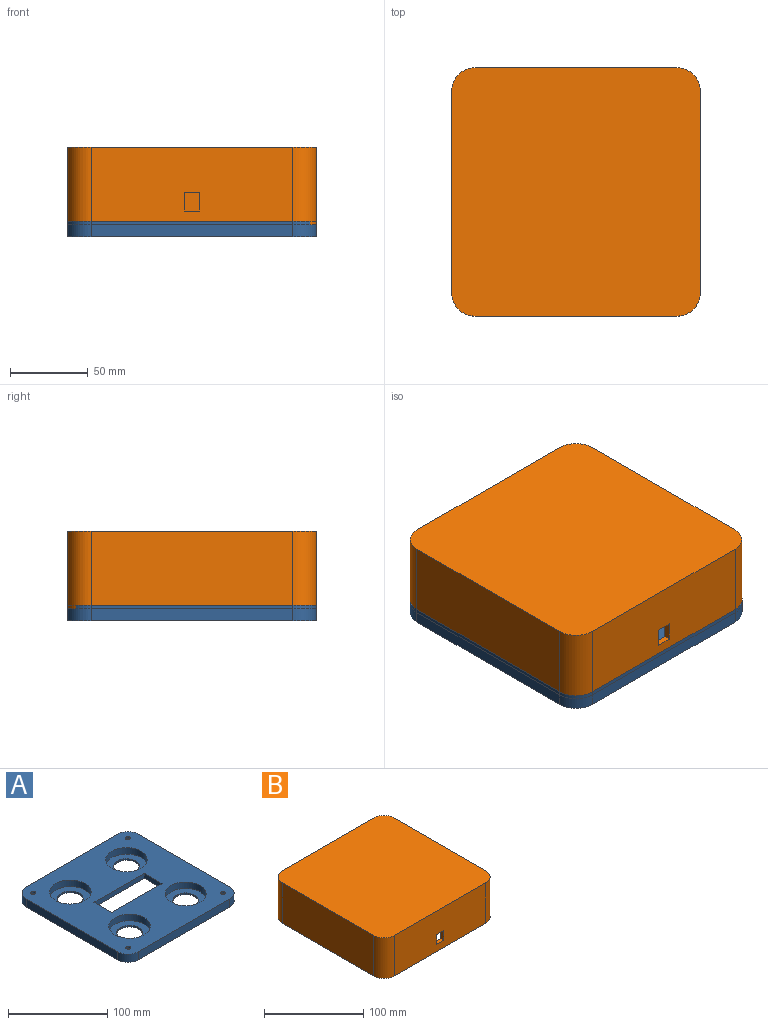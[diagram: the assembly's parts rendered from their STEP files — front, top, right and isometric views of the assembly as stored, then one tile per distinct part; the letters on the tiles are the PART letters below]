
ASSEMBLY  parts=2 mates=1
PART A: 53 faces, bbox 160x160x10 mm
  f0: plane 7x4.86mm, normal (0,-1,0), area 14.8mm2, adj f25,f44,f45,f46,f47,f52
  f1: plane 7x4.81mm, normal (0,1,0), area 14.7mm2, adj f2,f25,f44,f46,f48,f52
  f2: plane 25.5x6mm, normal (1,0,0), area 77.2mm2, adj f1,f3,f6,f24,f46,f52
  f3: plane 71.5x6mm, normal (0,-1,0), area 428.9mm2, adj f2,f23,f24,f45,f46,f52
  f4: cylinder r=21mm len=2.5mm, axis (0,0,-1), area 1.2mm2, adj f25,f30
  f5: cylinder r=21mm len=1.77mm, axis (0,0,-1), area 0.4mm2, adj f25,f29
  f6: plane 71.5x6mm, normal (0,1,0), area 429mm2, adj f2,f23,f24,f52
  f7: plane 130x10mm, normal (1,0,0), area 1300mm2, adj f8,f14,f24,f25
  f8: cylinder r=15mm len=15mm, axis (0,0,-1), area 235.6mm2, adj f7,f9,f24,f25
  f9: plane 130x10mm, normal (0,1,0), area 1300mm2, adj f8,f10,f24,f25
  f10: cylinder r=15mm len=15mm, axis (0,0,-1), area 235.6mm2, adj f9,f11,f24,f25
  f11: plane 130x10mm, normal (-1,0,0), area 1300mm2, adj f10,f12,f24,f25
  f12: cylinder r=15mm len=15mm, axis (0,0,-1), area 235.6mm2, adj f11,f13,f24,f25
  f13: plane 130x10mm, normal (0,-1,0), area 1300mm2, adj f12,f14,f24,f25
  f14: cylinder r=15mm len=15mm, axis (0,0,-1), area 235.6mm2, adj f7,f13,f24,f25
  f15: cylinder r=2.5mm len=5mm, axis (0,0,-1), area 39.3mm2, adj f24,f37
  f16: cylinder r=2.5mm len=5mm, axis (0,0,-1), area 39.3mm2, adj f24,f41
  f17: cylinder r=2.5mm len=5mm, axis (0,0,-1), area 39.3mm2, adj f24,f43
  f18: cylinder r=20.75mm len=41.5mm, axis (0,0,-1), area 1043mm2, adj f24,f34
  f19: cylinder r=21mm len=42mm, axis (0,0,-1), area 1055.6mm2, adj f24,f28
  f20: cylinder r=21mm len=42mm, axis (0,0,-1), area 1055.6mm2, adj f24,f26
  f21: cylinder r=21mm len=42mm, axis (0,0,-1), area 1055.6mm2, adj f24,f32
  f22: cylinder r=2.5mm len=5mm, axis (0,0,-1), area 39.3mm2, adj f24,f39
  f23: plane 25.5x6mm, normal (-1,0,0), area 153mm2, adj f3,f6,f24,f52
  f24: plane 160x160mm, normal (0,0,1), area 17996.1mm2, adj f2,f3,f6,f7,f8,f9,f10,f11
  f25: plane 160x160mm, normal (0,0,-1), area 20256.1mm2, adj f0,f1,f4,f5,f7,f8,f9,f10
  f26: plane 42x42mm, normal (0,0,1), area 863mm2, adj f20,f27
  f27: cone r=13mm half-angle=3deg, axis (0,0,-1), area 162.9mm2, adj f25,f26
  f28: plane 42x42mm, normal (0,0,1), area 863mm2, adj f19,f31
  f29: plane 1.77x0.36mm, normal (-0.04,-1,-0.05), area 0.4mm2, adj f5,f25
  f30: plane 2.5x0.71mm, normal (0.06,-1,-0.05), area 1.2mm2, adj f4,f25
  f31: cone r=13mm half-angle=3deg, axis (0,0,-1), area 162.9mm2, adj f25,f28
  f32: plane 42x42mm, normal (0,0,1), area 863mm2, adj f21,f33
  f33: cone r=13mm half-angle=3deg, axis (0,0,-1), area 162.9mm2, adj f25,f32
  f34: plane 41.5x41.5mm, normal (0,0,1), area 830.2mm2, adj f18,f35
  f35: cone r=13mm half-angle=3deg, axis (0,0,-1), area 162.9mm2, adj f25,f34
  f36: cylinder r=1.5mm len=7.5mm, axis (0,0,-1), area 70.7mm2, adj f25,f37
  f37: plane 5x5mm, normal (0,0,1), area 12.6mm2, adj f15,f36
  f38: cylinder r=1.5mm len=7.5mm, axis (0,0,-1), area 70.7mm2, adj f25,f39
  f39: plane 5x5mm, normal (0,0,1), area 12.6mm2, adj f22,f38
  f40: cylinder r=1.5mm len=7.5mm, axis (0,0,-1), area 70.7mm2, adj f25,f41
  f41: plane 5x5mm, normal (0,0,1), area 12.6mm2, adj f16,f40
  f42: cylinder r=1.5mm len=7.5mm, axis (0,0,-1), area 70.7mm2, adj f25,f43
  f43: plane 5x5mm, normal (0,0,1), area 12.6mm2, adj f17,f42
  f44: plane 25.33x7mm, normal (1,0,0), area 177.3mm2, adj f0,f1,f25,f46
  f45: plane 3x0.07mm, normal (-1,0,0), area 0.2mm2, adj f0,f3,f46,f52
  f46: plane 25.33x4.86mm, normal (0,0,-1), area 121.9mm2, adj f0,f1,f2,f3,f44,f45
  f47: plane 5.68x4mm, normal (1,0,0), area 22.7mm2, adj f0,f25,f51,f52
  f48: plane 5.99x4mm, normal (1,0,0), area 24mm2, adj f1,f25,f49,f52
  f49: plane 81x4mm, normal (0,1,0), area 324mm2, adj f25,f48,f50,f52
  f50: plane 37x4mm, normal (-1,0,0), area 148mm2, adj f25,f49,f51,f52
  f51: plane 81x4mm, normal (0,-1,0), area 324mm2, adj f25,f47,f50,f52
  f52: plane 81x37mm, normal (0,0,-1), area 1053.4mm2, adj f0,f1,f2,f3,f6,f23,f45,f47
PART B: 43 faces, bbox 160x160x50 mm
  f0: plane 122x40mm, normal (0,1,0), area 4760mm2, adj f8,f9,f25,f26,f27,f28,f29,f42
  f1: plane 122x40mm, normal (0,-1,0), area 4880mm2, adj f2,f15,f25,f42
  f2: cylinder r=15mm len=40mm, axis (0,0,-1), area 69.7mm2, adj f1,f3,f25,f30,f42
  f3: cylinder r=9.46mm len=14.3mm, axis (0,0,-1), area 247.6mm2, adj f2,f4,f32,f42
  f4: cylinder r=15mm len=40mm, axis (0,0,-1), area 87.1mm2, adj f3,f5,f25,f30,f42
  f5: plane 122x40mm, normal (-1,0,0), area 4880mm2, adj f4,f6,f25,f42
  f6: cylinder r=15mm len=40mm, axis (0,0,-1), area 87.1mm2, adj f5,f7,f25,f33,f42
  f7: cylinder r=9.46mm len=14.3mm, axis (0,0,-1), area 247.6mm2, adj f6,f8,f35,f42
  f8: cylinder r=15mm len=40mm, axis (0,0,-1), area 69.7mm2, adj f0,f7,f25,f33,f42
  f9: cylinder r=15mm len=40mm, axis (0,0,-1), area 69.7mm2, adj f0,f10,f25,f39,f42
  f10: cylinder r=9.46mm len=14.3mm, axis (0,0,-1), area 247.6mm2, adj f9,f11,f41,f42
  f11: cylinder r=15mm len=40mm, axis (0,0,-1), area 87.1mm2, adj f10,f12,f25,f39,f42
  f12: plane 122x40mm, normal (1,0,0), area 4880mm2, adj f11,f13,f25,f42
  f13: cylinder r=15mm len=40mm, axis (0,0,-1), area 87.1mm2, adj f12,f14,f25,f36,f42
  f14: cylinder r=9.46mm len=14.3mm, axis (0,0,-1), area 247.6mm2, adj f13,f15,f38,f42
  f15: cylinder r=15mm len=40mm, axis (0,0,-1), area 69.7mm2, adj f1,f14,f25,f36,f42
  f16: plane 130x50mm, normal (0,-1,0), area 6380mm2, adj f21,f22,f24,f25,f26,f27,f28,f29
  f17: cylinder r=15mm len=50mm, axis (0,0,-1), area 1178.1mm2, adj f18,f23,f24,f25
  f18: plane 130x50mm, normal (0,1,0), area 6500mm2, adj f17,f19,f24,f25
  f19: cylinder r=15mm len=50mm, axis (0,0,-1), area 1178.1mm2, adj f18,f20,f24,f25
  f20: plane 130x50mm, normal (-1,0,0), area 6500mm2, adj f19,f21,f24,f25
  f21: cylinder r=15mm len=50mm, axis (0,0,-1), area 1178.1mm2, adj f16,f20,f24,f25
  f22: cylinder r=15mm len=50mm, axis (0,0,-1), area 1178.1mm2, adj f16,f23,f24,f25
  f23: plane 130x50mm, normal (1,0,0), area 6500mm2, adj f17,f22,f24,f25
  f24: plane 160x160mm, normal (0,0,1), area 25406.9mm2, adj f16,f17,f18,f19,f20,f21,f22,f23
  f25: plane 160x160mm, normal (0,0,-1), area 3368.5mm2, adj f0,f1,f2,f4,f5,f6,f8,f9
  f26: plane 10x4mm, normal (0,0,-1), area 40mm2, adj f0,f16,f27,f29
  f27: plane 12x4mm, normal (1,0,0), area 48mm2, adj f0,f16,f26,f28
  f28: plane 10x4mm, normal (0,0,1), area 40mm2, adj f0,f16,f27,f29
  f29: plane 12x4mm, normal (-1,0,0), area 48mm2, adj f0,f16,f26,f28
  f30: cylinder r=9.46mm len=30mm, axis (0,0,-1), area 1039.4mm2, adj f2,f4,f25,f32
  f31: cylinder r=1.45mm len=30mm, axis (0,0,-1), area 273.3mm2, adj f25,f32
  f32: plane 18.91x18.91mm, normal (0,0,1), area 274.2mm2, adj f3,f30,f31
  f33: cylinder r=9.46mm len=30mm, axis (0,0,-1), area 1039.4mm2, adj f6,f8,f25,f35
  f34: cylinder r=1.45mm len=30mm, axis (0,0,-1), area 273.3mm2, adj f25,f35
  f35: plane 18.91x18.91mm, normal (0,0,1), area 274.2mm2, adj f7,f33,f34
  f36: cylinder r=9.46mm len=30mm, axis (0,0,-1), area 1039.4mm2, adj f13,f15,f25,f38
  f37: cylinder r=1.45mm len=30mm, axis (0,0,-1), area 273.3mm2, adj f25,f38
  f38: plane 18.91x18.91mm, normal (0,0,1), area 274.2mm2, adj f14,f36,f37
  f39: cylinder r=9.46mm len=30mm, axis (0,0,-1), area 1039.4mm2, adj f9,f11,f25,f41
  f40: cylinder r=1.45mm len=30mm, axis (0,0,-1), area 273.3mm2, adj f25,f41
  f41: plane 18.91x18.91mm, normal (0,0,1), area 274.2mm2, adj f10,f39,f40
  f42: plane 154.47x154.09mm, normal (0,0,-1), area 23135.3mm2, adj f0,f1,f2,f3,f4,f5,f6,f7
PLACE A t=(-67.61,19,54.57)mm
PLACE B t=(-67.58,19.03,62.07)mm
MATE fastened A.f15 <-> B.f14  axis (0,0,1) through (-135.17,86.81,62.07)mm
